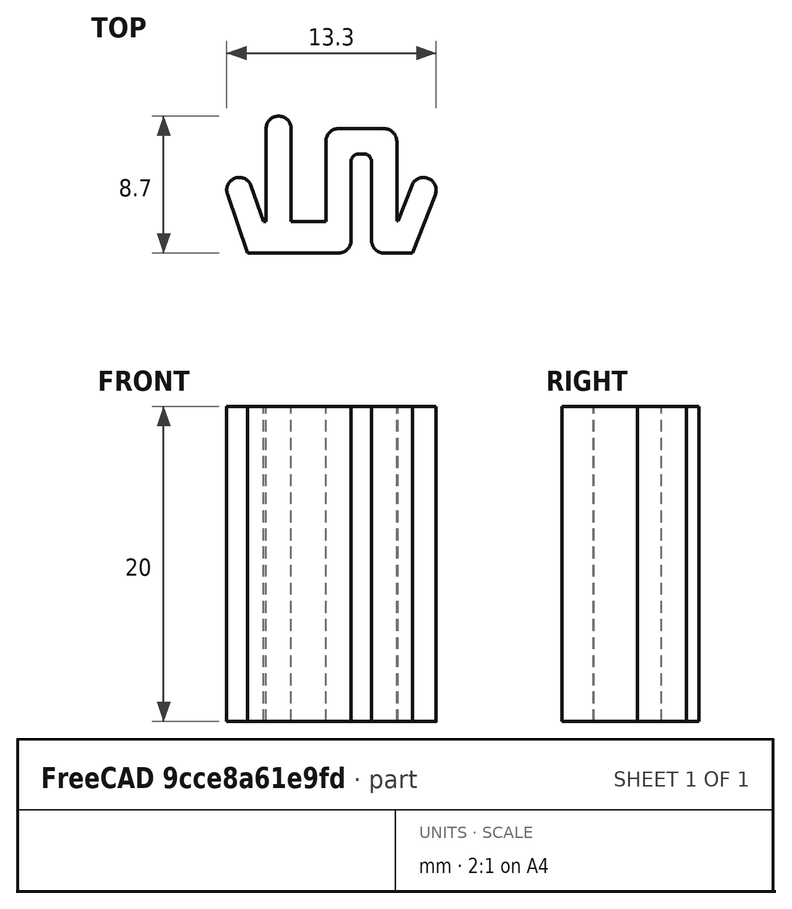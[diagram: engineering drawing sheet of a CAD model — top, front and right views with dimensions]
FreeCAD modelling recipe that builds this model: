
FCSTD DOCUMENT  (FreeCAD 0.21R33668 +7 (Git))
Label: rail-insert-v
License: All rights reserved
LicenseURL: http://en.wikipedia.org/wiki/All_rights_reserved
objects: Sketcher::SketchObject×1, PartDesign::Pad×1, PartDesign::Body×1
note: 4 computed .brp shape members not serialized (recipe doc carries the construction recipe); baked Part::Feature solids carry a one-line shape summary decoded from their .brp

FEATURE [Sketcher::SketchObject] Sketch
  FullyConstrained = false
  MapMode = 5
  Support = -> [XY_Plane]
  sketch-geometry (46):
    g0: LineSegment StartX=-7.85 StartY=0 StartZ=0 EndX=7.85 EndY=0 EndZ=0
    g1: LineSegment StartX=7.85 StartY=0 StartZ=0 EndX=7.85 EndY=7.2 EndZ=0
    g2: LineSegment StartX=7.85 StartY=7.2 StartZ=0 EndX=4.15 EndY=7.2 EndZ=0
    g3: LineSegment StartX=4.15 StartY=7.2 StartZ=0 EndX=4.15 EndY=6 EndZ=0
    g4: LineSegment StartX=4.15 StartY=6 StartZ=0 EndX=6.65 EndY=6 EndZ=0
    g5: LineSegment StartX=6.65 StartY=6 StartZ=0 EndX=6.65 EndY=1.2 EndZ=0
    g6: LineSegment StartX=6.65 StartY=1.2 StartZ=0 EndX=-6.65 EndY=1.2 EndZ=0
    g7: LineSegment StartX=-6.65 StartY=1.2 StartZ=0 EndX=-6.65 EndY=6 EndZ=0
    g8: LineSegment StartX=-6.65 StartY=6 StartZ=0 EndX=-4.15 EndY=6 EndZ=0
    g9: LineSegment StartX=-4.15 StartY=6 StartZ=0 EndX=-4.15 EndY=7.2 EndZ=0
    g10: LineSegment StartX=-4.15 StartY=7.2 StartZ=0 EndX=-7.85 EndY=7.2 EndZ=0
    g11: LineSegment StartX=-7.85 StartY=7.2 StartZ=0 EndX=-7.85 EndY=0 EndZ=0
    g12: LineSegment StartX=5.14036 StartY=1.2 StartZ=0 EndX=6.59476 EndY=4.90787 EndZ=0
    g13: LineSegment StartX=-5.33137 StartY=1.2 StartZ=0 EndX=-6.6072 EndY=4.94182 EndZ=0
    g14: LineSegment StartX=-5.0928 StartY=5.45818 StartZ=0 EndX=-4.3256 EndY=3.20805 EndZ=0
    g15: LineSegment StartX=-4.3256 StartY=3.20805 StartZ=0 EndX=-4.15 EndY=3.20805 EndZ=0
    g16: LineSegment StartX=-4.15 StartY=3.20805 StartZ=0 EndX=-4.15 EndY=9.1 EndZ=0
    g17: LineSegment StartX=-4.15 StartY=9.1 StartZ=0 EndX=-2.55 EndY=9.1 EndZ=0
    g18: LineSegment StartX=-2.55 StartY=9.1 StartZ=0 EndX=-2.55 EndY=3.19993 EndZ=0
    g19: LineSegment StartX=-2.55 StartY=3.19993 StartZ=0 EndX=-0.35 EndY=3.19993 EndZ=0
    g20: LineSegment StartX=-0.35 StartY=3.19993 StartZ=0 EndX=-0.35 EndY=8.3 EndZ=0
    g21: LineSegment StartX=0.45 StartY=9.1 StartZ=0 EndX=3.35 EndY=9.1 EndZ=0
    g22: LineSegment StartX=4.15 StartY=8.3 StartZ=0 EndX=4.15 EndY=3.23141 EndZ=0
    g23: LineSegment StartX=4.15 StartY=3.23141 StartZ=0 EndX=4.21849 EndY=3.23141 EndZ=0
    g24: LineSegment StartX=4.21849 StartY=3.23141 StartZ=0 EndX=5.10524 EndY=5.49213 EndZ=0
    g25: ArcOfCircle CenterX=-5.85 CenterY=5.2 CenterZ=0 NormalX=0 NormalY=0 NormalZ=1 AngleXU=0 Radius=0.8 StartAngle=0.328601 EndAngle=3.47019
    g26: ArcOfCircle CenterX=5.85 CenterY=5.2 CenterZ=0 NormalX=0 NormalY=0 NormalZ=1 AngleXU=0 Radius=0.8 StartAngle=5.90938 EndAngle=9.05098
    g27: ArcOfCircle CenterX=-3.35 CenterY=9.1 CenterZ=0 NormalX=0 NormalY=0 NormalZ=1 AngleXU=0 Radius=0.8 StartAngle=7e-16 EndAngle=3.14159
    g28: LineSegment StartX=-5.33137 StartY=1.2 StartZ=0 EndX=0.449979 EndY=1.19985 EndZ=0
    g29: LineSegment StartX=1.25 StartY=1.19983 StartZ=0 EndX=2.55 EndY=1.19981 EndZ=0
    g30: LineSegment StartX=3.35006 StartY=1.19987 StartZ=0 EndX=5.14036 EndY=1.2 EndZ=0
    g31: LineSegment StartX=1.25 StartY=1.99985 StartZ=0 EndX=1.25 EndY=7.00909 EndZ=0
    g32: LineSegment StartX=1.74091 StartY=7.5 StartZ=0 EndX=2.05909 EndY=7.5 EndZ=0
    g33: LineSegment StartX=2.55 StartY=7.00909 StartZ=0 EndX=2.55 EndY=1.99987 EndZ=0
    g34: ArcOfCircle CenterX=0.45 CenterY=8.3 CenterZ=0 NormalX=0 NormalY=0 NormalZ=1 AngleXU=0 Radius=0.8 StartAngle=1.5708 EndAngle=3.14159
    g35: GeomPoint X=-0.35 Y=9.1 Z=0
    g36: ArcOfCircle CenterX=3.35 CenterY=8.3 CenterZ=0 NormalX=0 NormalY=0 NormalZ=1 AngleXU=0 Radius=0.8 StartAngle=-9e-16 EndAngle=1.5708
    g37: GeomPoint X=4.15 Y=9.1 Z=0
    g38: ArcOfCircle CenterX=0.45 CenterY=1.99985 CenterZ=0 NormalX=0 NormalY=0 NormalZ=1 AngleXU=0 Radius=0.8 StartAngle=4.71236 EndAngle=6.28319
    g39: GeomPoint X=1.25 Y=1.19983 Z=0
    g40: ArcOfCircle CenterX=3.35 CenterY=1.99987 CenterZ=0 NormalX=0 NormalY=0 NormalZ=1 AngleXU=0 Radius=0.8 StartAngle=3.14159 EndAngle=4.71246
    g41: GeomPoint X=2.55 Y=1.19981 Z=0
    g42: ArcOfCircle CenterX=1.74091 CenterY=7.00909 CenterZ=0 NormalX=0 NormalY=0 NormalZ=1 AngleXU=0 Radius=0.490913 StartAngle=1.5708 EndAngle=3.14159
    g43: GeomPoint X=1.25 Y=7.5 Z=0
    g44: ArcOfCircle CenterX=2.05909 CenterY=7.00909 CenterZ=0 NormalX=0 NormalY=0 NormalZ=1 AngleXU=0 Radius=0.490913 StartAngle=0 EndAngle=1.5708
    g45: GeomPoint X=2.55 Y=7.5 Z=0
  constraints (114):
    c: PointOnObject(g0,g-1)
    c: Coincident(g0,g1)
    c: Vertical(g1)
    c: Coincident(g1,g2)
    c: Horizontal(g2)
    c: Coincident(g2,g3)
    c: Vertical(g3)
    c: Coincident(g3,g4)
    c: Horizontal(g4)
    c: Coincident(g4,g5)
    c: Vertical(g5)
    c: Coincident(g5,g6)
    c: Horizontal(g6)
    c: Coincident(g6,g7)
    c: Vertical(g7)
    c: Coincident(g7,g8)
    c: Horizontal(g8)
    c: Coincident(g8,g9)
    c: Vertical(g9)
    c: Coincident(g9,g10)
    c: Horizontal(g10)
    c: Coincident(g10,g11)
    c: Coincident(g11,g0)
    c: Vertical(g11)
    c: Equal(g9,g3)
    c: Equal(g7,g5)
    c: Equal(g4,g8)
    c: Equal(g2,g10)
    c: Symmetric(g0,g0,g-1)
    c: DistanceX(g0,g0) = 15.7
    c: Distance(g5,g1) = 1.2
    c: Distance(g5,g0) = 1.2
    c: Distance(g11) = 7.2
    c: Distance(g7,g10) = 1.2
    c: Distance(g10) = 3.7
    c: PointOnObject(g28,g6)
    c: PointOnObject(g30,g6)
    c: Coincident(g30,g12)
    c: Coincident(g28,g13)
    c: Coincident(g14,g15)
    c: Horizontal(g15)
    c: Coincident(g15,g16)
    c: Vertical(g16)
    c: Coincident(g16,g17)
    c: Horizontal(g17)
    c: Coincident(g17,g18)
    c: Vertical(g18)
    c: Coincident(g18,g19)
    c: Horizontal(g19)
    c: Coincident(g19,g20)
    c: Vertical(g20)
    c: Horizontal(g21)
    c: Vertical(g22)
    c: Coincident(g22,g23)
    c: Horizontal(g23)
    c: Coincident(g23,g24)
    c: Tangent(g25,g14) = 1.5708
    c: Tangent(g25,g13) = 1.5708
    c: Tangent(g26,g24) = 1.5708
    c: Tangent(g26,g12) = -1.5708
    c: Equal(g25,g26)
    c: Parallel(g14,g13)
    c: Parallel(g24,g12)
    c: Tangent(g25,g8)
    c: Tangent(g25,g7)
    c: Tangent(g26,g4)
    c: Tangent(g26,g5)
    c: PointOnObject(g8,g16)
    c: PointOnObject(g3,g22)
    c: DistanceX(g17,g17) = 1.6
    c: DistanceX(g19,g19) = 2.2
    c: Distance(g37,g2) = 1.9
    c: Coincident(g27,g17)
    c: Tangent(g27,g16) = 1.5708
    c: Coincident(g39,g29)
    c: Distance(g18,g28) = 2
    c: Coincident(g29,g41)
    c: Vertical(g31)
    c: Horizontal(g32)
    c: Vertical(g33)
    c: Distance(g43,g20) = 1.6
    c: Distance(g45,g22) = 1.6
    c: Distance(g45,g21) = 1.6
    c: PointOnObject(g35,g21)
    c: PointOnObject(g35,g20)
    c: Tangent(g21,g34) = 1.5708
    c: Tangent(g20,g34) = 1.5708
    c: PointOnObject(g37,g21)
    c: PointOnObject(g37,g22)
    c: Tangent(g21,g36) = 1.5708
    c: Tangent(g22,g36) = 1.5708
    c: Equal(g36,g34)
    c: Equal(g34,g27)
    c: Equal(g36,g26)
    c: PointOnObject(g39,g31)
    c: PointOnObject(g39,g28)
    c: Tangent(g31,g38) = -1.5708
    c: Tangent(g28,g38) = -1.5708
    c: PointOnObject(g41,g30)
    c: PointOnObject(g41,g33)
    c: Tangent(g30,g40) = -1.5708
    c: Tangent(g33,g40) = -1.5708
    c: Equal(g38,g40)
    c: Equal(g40,g36)
    c: PointOnObject(g43,g32)
    c: PointOnObject(g43,g31)
    c: Tangent(g32,g42) = 1.5708
    c: Tangent(g31,g42) = 1.5708
    c: PointOnObject(g45,g33)
    c: PointOnObject(g45,g32)
    c: Tangent(g33,g44) = 1.5708
    c: Tangent(g32,g44) = 1.5708
    c: Equal(g42,g44)
    c: PointOnObject(g27,g21)
FEATURE [PartDesign::Pad] Pad
  Direction = (0,0,1)
  Length = 20
  Length2 = 10
  Profile = -> Sketch
  ReferenceAxis = -> Sketch [N_Axis]
  Type = 0
FEATURE [PartDesign::Body] Body
  Group = -> [Sketch,Pad]
  Origin = -> Origin
  Tip = -> Pad
